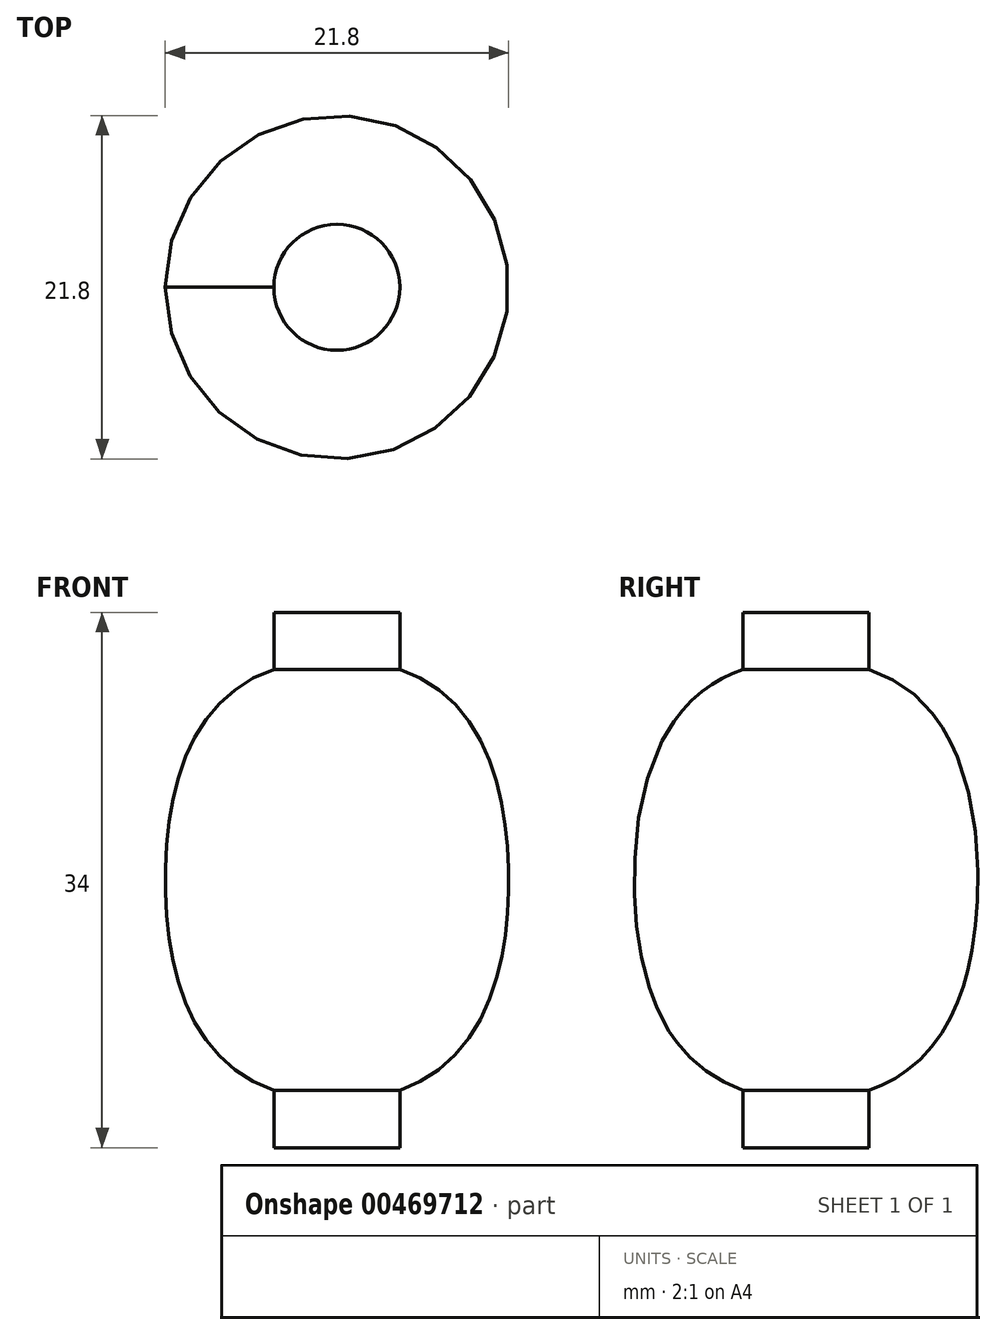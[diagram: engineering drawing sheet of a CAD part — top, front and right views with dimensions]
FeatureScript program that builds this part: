
annotation { "Feature Type Name" : "Feature", "Feature Type Description" : "" }
export const myFeature = defineFeature(function(context is Context, id is Id, definition is map)
    precondition{}
    {
        {
            var Q0;
            Q0=qCreatedBy(makeId("Front.planeOp"),FACE);
            var sketch = newSketch(context, id + "F0", { "sketchPlane" : qUnion([Q0])});
            skFitSpline(sketch, "E0", {"points": [v(0, 14) * mm, v(-10.9, 0) * mm, v(0, -14) * mm], "startDerivative": vector(-52.06, 0) * mm, "endDerivative": vector(52.06, -0.48) * mm});
            skLineSegment(sketch, "E1", {"start": v(0, 17) * mm, "end": v(-4, 17) * mm});
            skLineSegment(sketch, "E2", {"start": v(-4, 17) * mm, "end": v(-4, 13.39) * mm});
            skLineSegment(sketch, "E3", {"start": v(0, -17) * mm, "end": v(0, 17) * mm});
            skLineSegment(sketch, "E4", {"start": v(0, -17) * mm, "end": v(-4, -17) * mm});
            skLineSegment(sketch, "E5", {"start": v(-4, -17) * mm, "end": v(-4, -13.36) * mm});
            skSolve(sketch);
        }
        {
            var Q0;
            {var subQ0=sQuery(id+"F0.wireOp",EDGE,"E3");var subQ1=sQuery(id+"F0.wireOp",EDGE,"E0");var subQ2=makeQuery(id+"F0.imprint","INTERSECT",VERTEX,{"disambiguationData":[OD(0.0)],"derivedFrom":[subQ1,subQ0]});Q0=makeQuery(id+"F0.imprint","IMPRINT",FACE,{"disambiguationData":[TD([[makeQuery(id+"F0.imprint","IMPRINT",EDGE,{"disambiguationData":[TD([[subQ2,-1.0]])],"derivedFrom":subQ1}),1.0]])]});}
            var Q1;
            {var subQ4=sQuery(id+"F0.wireOp",EDGE,"E1");Q1=makeQuery(id+"F0.imprint","IMPRINT",FACE,{"disambiguationData":[TD([[makeQuery(id+"F0.imprint","IMPRINT",EDGE,{"derivedFrom":subQ4}),1.0]])]});}
            var Q2;
            {var subQ4=sQuery(id+"F0.wireOp",EDGE,"E4");Q2=makeQuery(id+"F0.imprint","IMPRINT",FACE,{"disambiguationData":[TD([[makeQuery(id+"F0.imprint","IMPRINT",EDGE,{"derivedFrom":subQ4}),-1.0]])]});}
            var Q3;
            Q3=sQuery(id+"F0.wireOp",EDGE,"E3");
            revolve(context, id + "F1", {"entities" : qUnion([Q0, Q1, Q2]), "axis" : qUnion([Q3]), "revolveType" : RevolveType.FULL});
        }
    });
